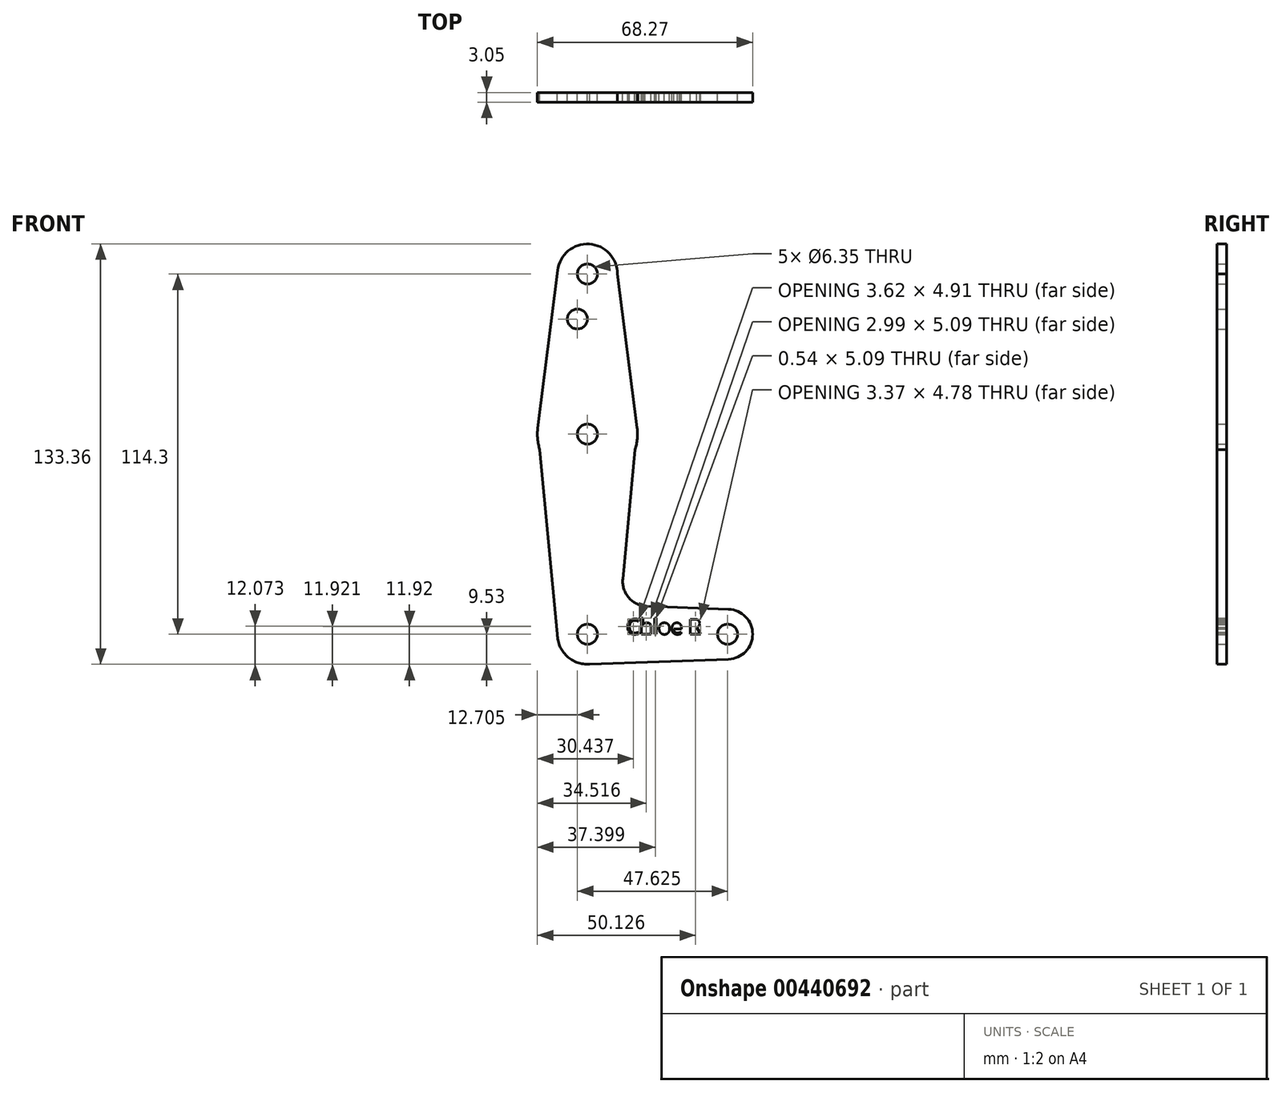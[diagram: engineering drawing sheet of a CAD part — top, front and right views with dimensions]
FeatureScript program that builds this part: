
annotation { "Feature Type Name" : "Feature", "Feature Type Description" : "" }
export const myFeature = defineFeature(function(context is Context, id is Id, definition is map)
    precondition{}
    {
        {
            var Q0;
            Q0=qCreatedBy(makeId("Front.planeOp"),FACE);
            var sketch = newSketch(context, id + "F0", { "sketchPlane" : qUnion([Q0])});
            skLineSegment(sketch, "E0", {"start": v(0, 0) * mm, "end": v(44.45, 0) * mm});
            skLineSegment(sketch, "E1", {"start": v(44.45, 0) * mm, "end": v(0, 0) * mm, "construction": true});
            skLineSegment(sketch, "E2", {"start": v(0, 0) * mm, "end": v(0, 114.3) * mm, "construction": true});
            skCircle(sketch, "E3", {"center": v(0, 114.3) * mm, "radius": 9.53 * mm});
            skCircle(sketch, "E4", {"center": v(0, 63.5) * mm, "radius": 15.88 * mm});
            skCircle(sketch, "E5", {"center": v(0, 0) * mm, "radius": 9.53 * mm});
            skCircle(sketch, "E6", {"center": v(44.45, 0) * mm, "radius": 7.94 * mm});
            skLineSegment(sketch, "E7", {"start": v(-9.45, 115.5) * mm, "end": v(-15.75, 65.48) * mm});
            skLineSegment(sketch, "E8", {"start": v(-15.75, 65.48) * mm, "end": v(-9.53, 0) * mm});
            skLineSegment(sketch, "E9", {"start": v(9.53, 114.3) * mm, "end": v(15.75, 65.5) * mm});
            skLineSegment(sketch, "E10", {"start": v(15.75, 65.5) * mm, "end": v(11.22, 17.55) * mm});
            skLineSegment(sketch, "E11", {"start": v(0, -9.53) * mm, "end": v(44.73, -7.93) * mm});
            skLineSegment(sketch, "E12", {"start": v(18.85, 8.85) * mm, "end": v(44.73, 7.93) * mm});
            skCircle(sketch, "E13", {"center": v(0, 114.3) * mm, "radius": 3.18 * mm});
            skCircle(sketch, "E14", {"center": v(0, 63.5) * mm, "radius": 3.18 * mm});
            skCircle(sketch, "E15", {"center": v(0, 0) * mm, "radius": 3.18 * mm});
            skCircle(sketch, "E16", {"center": v(44.45, 0) * mm, "radius": 3.18 * mm});
            skCircle(sketch, "E17", {"center": v(-3.17, 100.03) * mm, "radius": 3.18 * mm});
            skArc(sketch, "E18.filletArc", {"start": v(11.22, 17.55) * mm, "mid": v(13.16, 11.55) * mm, "end": v(18.85, 8.85) * mm});
            skText(sketch, "E19", { "text": "Chloe R", "fontName": "OpenSans-Regular.ttf"});
            const initialGuessF0  = {"E19": [0.01234, 0, 1, 0, 0.00482]};
            skSetInitialGuess(sketch, initialGuessF0);
            skSolve(sketch);
        }
        {
            var Q0;
            Q0 = qSketchRegion(id + "F0", true);
            extrude(context, id + "F1", {"entities" : qUnion([Q0]), "depth" : 3.05 * mm});
        }
    });
